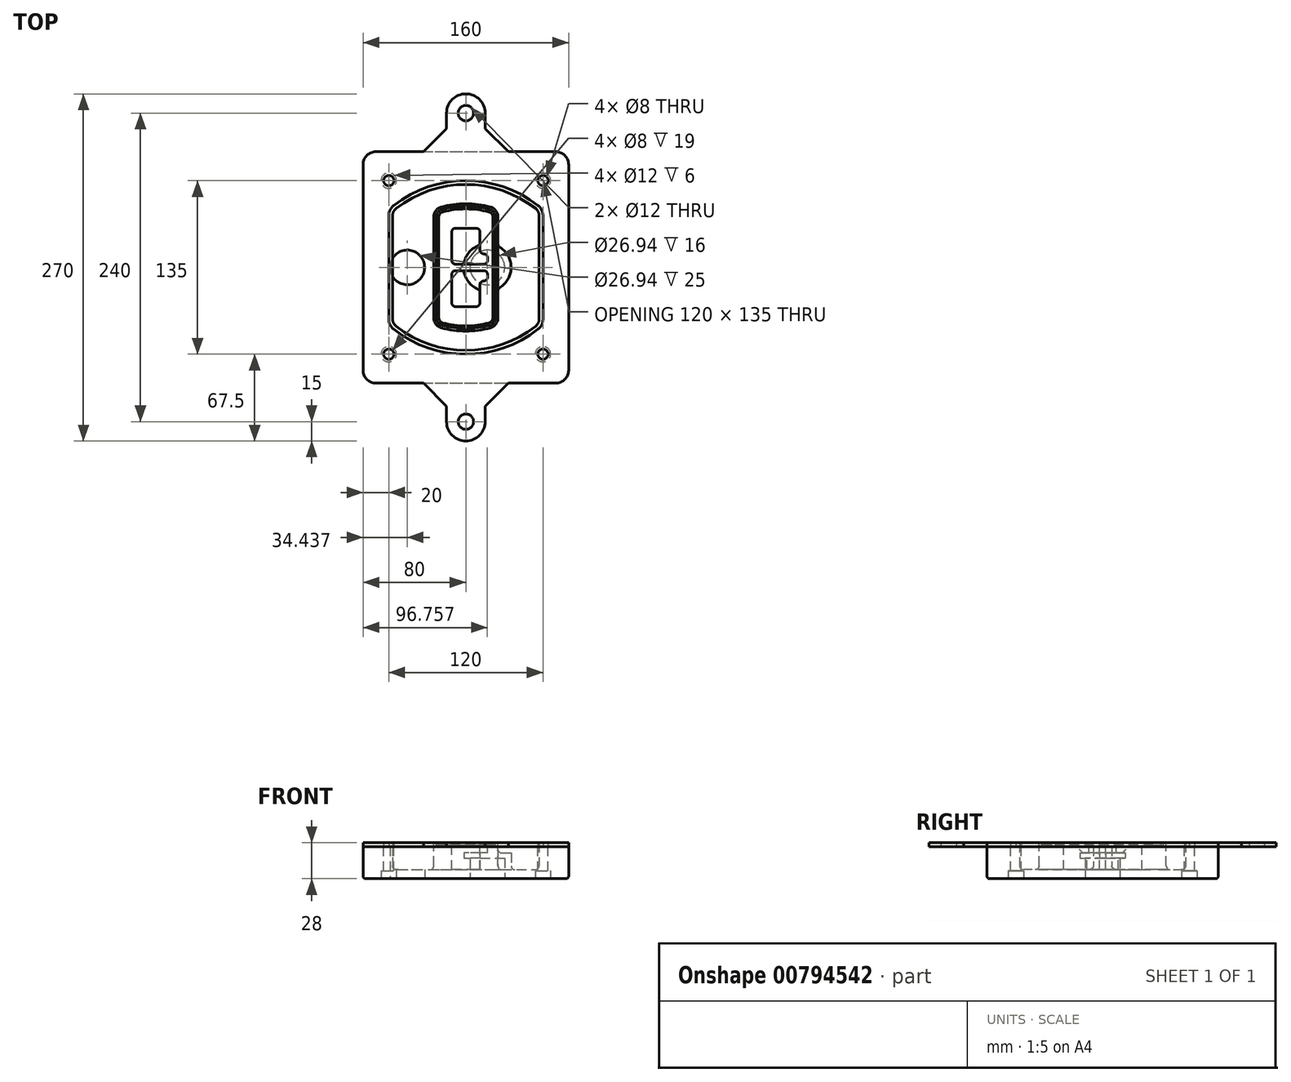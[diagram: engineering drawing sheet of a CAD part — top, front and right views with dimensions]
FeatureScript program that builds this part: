
annotation { "Feature Type Name" : "Feature", "Feature Type Description" : "" }
export const myFeature = defineFeature(function(context is Context, id is Id, definition is map)
    precondition{}
    {
        {
            var Q0;
            Q0=qCreatedBy(makeId("Top.planeOp"),FACE);
            var sketch = newSketch(context, id + "F0", { "sketchPlane" : qUnion([Q0])});
            skPoint(sketch, "E0.rect.middle", {"position": v(0, 0) * mm});
            skLineSegment(sketch, "E1.bottom", {"start": v(-70, -90) * mm, "end": v(70, -90) * mm});
            skLineSegment(sketch, "E1.top", {"start": v(-70, 90) * mm, "end": v(70, 90) * mm});
            skLineSegment(sketch, "E1.left", {"start": v(-80, -80) * mm, "end": v(-80, 80) * mm});
            skLineSegment(sketch, "E1.right", {"start": v(80, -80) * mm, "end": v(80, 80) * mm});
            skLineSegment(sketch, "E2", {"start": v(-80, 90) * mm, "end": v(80, -90) * mm, "construction": true});
            skLineSegment(sketch, "E3", {"start": v(80, 90) * mm, "end": v(-80, -90) * mm, "construction": true});
            skCircle(sketch, "E4", {"center": v(-60, 67.5) * mm, "radius": 4 * mm});
            skCircle(sketch, "E5", {"center": v(60, 67.5) * mm, "radius": 4 * mm});
            skCircle(sketch, "E6", {"center": v(60, -67.5) * mm, "radius": 4 * mm});
            skCircle(sketch, "E7", {"center": v(-60, -67.5) * mm, "radius": 4 * mm});
            skLineSegment(sketch, "E8", {"start": v(-60, 67.5) * mm, "end": v(60, 67.5) * mm, "construction": true});
            skLineSegment(sketch, "E9", {"start": v(60, 67.5) * mm, "end": v(60, -67.5) * mm, "construction": true});
            skLineSegment(sketch, "E10", {"start": v(60, -67.5) * mm, "end": v(-60, -67.5) * mm, "construction": true});
            skLineSegment(sketch, "E11", {"start": v(-60, -67.5) * mm, "end": v(-60, 67.5) * mm, "construction": true});
            skLineSegment(sketch, "E12", {"start": v(-60, 40.3) * mm, "end": v(-60, -40.3) * mm});
            skLineSegment(sketch, "E13", {"start": v(60, 40.3) * mm, "end": v(60, -40.3) * mm});
            skArc(sketch, "E14", {"start": v(56.15, 48.18) * mm, "mid": v(0, 67.5) * mm, "end": v(-56.15, 48.18) * mm});
            skArc(sketch, "E15", {"start": v(-56.15, -48.18) * mm, "mid": v(0, -67.5) * mm, "end": v(56.15, -48.18) * mm});
            skLineSegment(sketch, "E16", {"start": v(-60, 0) * mm, "end": v(60, 0) * mm, "construction": true});
            skPoint(sketch, "E17.visualSharp", {"position": v(-60, -45) * mm});
            skArc(sketch, "E17.filletArc", {"start": v(-60, -40.3) * mm, "mid": v(-58.99, -44.68) * mm, "end": v(-56.15, -48.18) * mm});
            skPoint(sketch, "E18.visualSharp", {"position": v(-60, 45) * mm});
            skArc(sketch, "E18.filletArc", {"start": v(-56.15, 48.18) * mm, "mid": v(-58.99, 44.68) * mm, "end": v(-60, 40.3) * mm});
            skPoint(sketch, "E19.visualSharp", {"position": v(60, 45) * mm});
            skArc(sketch, "E19.filletArc", {"start": v(60, 40.3) * mm, "mid": v(58.99, 44.68) * mm, "end": v(56.15, 48.18) * mm});
            skPoint(sketch, "E20.visualSharp", {"position": v(60, -45) * mm});
            skArc(sketch, "E20.filletArc", {"start": v(56.15, -48.18) * mm, "mid": v(58.99, -44.68) * mm, "end": v(60, -40.3) * mm});
            skPoint(sketch, "E21.visualSharp", {"position": v(-80, 90) * mm});
            skArc(sketch, "E21.filletArc", {"start": v(-70, 90) * mm, "mid": v(-77.07, 87.07) * mm, "end": v(-80, 80) * mm});
            skPoint(sketch, "E22.visualSharp", {"position": v(80, 90) * mm});
            skArc(sketch, "E22.filletArc", {"start": v(80, 80) * mm, "mid": v(77.07, 87.07) * mm, "end": v(70, 90) * mm});
            skPoint(sketch, "E23.visualSharp", {"position": v(80, -90) * mm});
            skArc(sketch, "E23.filletArc", {"start": v(70, -90) * mm, "mid": v(77.07, -87.07) * mm, "end": v(80, -80) * mm});
            skPoint(sketch, "E24.visualSharp", {"position": v(-80, -90) * mm});
            skArc(sketch, "E24.filletArc", {"start": v(-80, -80) * mm, "mid": v(-77.07, -87.07) * mm, "end": v(-70, -90) * mm});
            skArc(sketch, "E25.0", {"start": v(57, 40.3) * mm, "mid": v(56.3, 43.36) * mm, "end": v(54.3, 45.81) * mm});
            skLineSegment(sketch, "E25.1", {"start": v(57, 40.3) * mm, "end": v(57, -40.3) * mm});
            skArc(sketch, "E25.2", {"start": v(54.3, -45.81) * mm, "mid": v(56.3, -43.36) * mm, "end": v(57, -40.3) * mm});
            skArc(sketch, "E25.3", {"start": v(-54.3, -45.81) * mm, "mid": v(0, -64.5) * mm, "end": v(54.3, -45.81) * mm});
            skArc(sketch, "E25.4", {"start": v(-57, -40.3) * mm, "mid": v(-56.3, -43.36) * mm, "end": v(-54.3, -45.81) * mm});
            skArc(sketch, "E25.5", {"start": v(54.3, 45.81) * mm, "mid": v(0, 64.5) * mm, "end": v(-54.3, 45.81) * mm});
            skLineSegment(sketch, "E25.6", {"start": v(-57, 40.3) * mm, "end": v(-57, -40.3) * mm});
            skArc(sketch, "E25.7", {"start": v(-54.3, 45.81) * mm, "mid": v(-56.3, 43.36) * mm, "end": v(-57, 40.3) * mm});
            skArc(sketch, "E26.0", {"start": v(-58.62, 51.33) * mm, "mid": v(-62.58, 46.43) * mm, "end": v(-64, 40.3) * mm});
            skArc(sketch, "E26.1", {"start": v(58.62, 51.33) * mm, "mid": v(0, 71.5) * mm, "end": v(-58.62, 51.33) * mm});
            skArc(sketch, "E26.2", {"start": v(64, 40.3) * mm, "mid": v(62.58, 46.43) * mm, "end": v(58.62, 51.33) * mm});
            skLineSegment(sketch, "E26.3", {"start": v(64, 40.3) * mm, "end": v(64, -40.3) * mm});
            skArc(sketch, "E26.4", {"start": v(58.62, -51.33) * mm, "mid": v(62.58, -46.43) * mm, "end": v(64, -40.3) * mm});
            skLineSegment(sketch, "E26.5", {"start": v(-64, 40.3) * mm, "end": v(-64, -40.3) * mm});
            skArc(sketch, "E26.6", {"start": v(-58.62, -51.33) * mm, "mid": v(0, -71.5) * mm, "end": v(58.62, -51.33) * mm});
            skArc(sketch, "E26.7", {"start": v(-64, -40.3) * mm, "mid": v(-62.58, -46.43) * mm, "end": v(-58.62, -51.33) * mm});
            skSolve(sketch);
        }
        {
            var Q0;
            Q0=makeQuery(id+"F0.imprint","IMPRINT",FACE,{"disambiguationData":[TD([[makeQuery(id+"F0.imprint","IMPRINT",EDGE,{"derivedFrom":sQuery(id+"F0.wireOp",EDGE,"E1.bottom")}),1.0]])]});
            var Q1;
            Q1=makeQuery(id+"F0.imprint","IMPRINT",FACE,{"disambiguationData":[TD([[makeQuery(id+"F0.imprint","IMPRINT",EDGE,{"derivedFrom":sQuery(id+"F0.wireOp",EDGE,"E12")}),1.0]])]});
            var Q2;
            Q2=makeQuery(id+"F0.imprint","IMPRINT",FACE,{"disambiguationData":[TD([[makeQuery(id+"F0.imprint","IMPRINT",EDGE,{"derivedFrom":sQuery(id+"F0.wireOp",EDGE,"E25.0")}),1.0]])]});
            var Q3;
            Q3=makeQuery(id+"F0.imprint","IMPRINT",FACE,{"disambiguationData":[TD([[makeQuery(id+"F0.imprint","IMPRINT",EDGE,{"derivedFrom":sQuery(id+"F0.wireOp",EDGE,"E12")}),-1.0]])]});
            extrude(context, id + "F1", {"entities" : qUnion([Q0, Q1, Q2, Q3]), "oppositeDirection" : true, "depth" : 25 * mm});
        }
        {
            var Q0;
            Q0=makeQuery(id+"F0.imprint","IMPRINT",FACE,{"disambiguationData":[TD([[makeQuery(id+"F0.imprint","IMPRINT",EDGE,{"derivedFrom":sQuery(id+"F0.wireOp",EDGE,"E12")}),1.0]])]});
            extrude(context, id + "F2", {"entities" : qUnion([Q0]), "operationType" : NewBodyOperationType.ADD, "depth" : 3 * mm});
        }
        {
            var Q0;
            Q0=makeQuery(id+"F0.imprint","IMPRINT",FACE,{"disambiguationData":[TD([[makeQuery(id+"F0.imprint","IMPRINT",EDGE,{"derivedFrom":sQuery(id+"F0.wireOp",EDGE,"E25.0")}),1.0]])]});
            extrude(context, id + "F3", {"entities" : qUnion([Q0]), "operationType" : NewBodyOperationType.REMOVE, "oppositeDirection" : true, "depth" : 18 * mm});
        }
        {
            var Q0;
            Q0=makeQuery(id+"F2.opExtrude","CAP_FACE",FACE,{"disambiguationData":[OSD([sQuery(id+"F0.wireOp",EDGE,"E12"),sQuery(id+"F0.wireOp",EDGE,"E13"),sQuery(id+"F0.wireOp",EDGE,"E14"),sQuery(id+"F0.wireOp",EDGE,"E15"),sQuery(id+"F0.wireOp",EDGE,"E17.filletArc"),sQuery(id+"F0.wireOp",EDGE,"E18.filletArc"),sQuery(id+"F0.wireOp",EDGE,"E19.filletArc"),sQuery(id+"F0.wireOp",EDGE,"E20.filletArc"),sQuery(id+"F0.wireOp",EDGE,"E25.0"),sQuery(id+"F0.wireOp",EDGE,"E25.1"),sQuery(id+"F0.wireOp",EDGE,"E25.2"),sQuery(id+"F0.wireOp",EDGE,"E25.3"),sQuery(id+"F0.wireOp",EDGE,"E25.4"),sQuery(id+"F0.wireOp",EDGE,"E25.5"),sQuery(id+"F0.wireOp",EDGE,"E25.6"),sQuery(id+"F0.wireOp",EDGE,"E25.7")])],"isStart":false});
            var sketch = newSketch(context, id + "F4", { "sketchPlane" : qUnion([Q0])});
            skArc(sketch, "E27.0", {"start": v(-19.08, -46.97) * mm, "mid": v(0, -49.5) * mm, "end": v(19.08, -46.97) * mm});
            skArc(sketch, "E28.0", {"start": v(19.08, 46.97) * mm, "mid": v(0, 49.5) * mm, "end": v(-19.08, 46.97) * mm});
            skLineSegment(sketch, "E29", {"start": v(-25, 39.25) * mm, "end": v(-25, -39.25) * mm});
            skLineSegment(sketch, "E30", {"start": v(25, 39.25) * mm, "end": v(25, -39.25) * mm});
            skLineSegment(sketch, "E31", {"start": v(-25, 45.1) * mm, "end": v(25, 45.1) * mm, "construction": true});
            skLineSegment(sketch, "E32", {"start": v(-25, -45.1) * mm, "end": v(25, -45.1) * mm, "construction": true});
            skPoint(sketch, "E33.visualSharp", {"position": v(-25, 45.1) * mm});
            skArc(sketch, "E33.filletArc", {"start": v(-19.08, 46.97) * mm, "mid": v(-23.35, 44.11) * mm, "end": v(-25, 39.25) * mm});
            skPoint(sketch, "E34.visualSharp", {"position": v(25, 45.1) * mm});
            skArc(sketch, "E34.filletArc", {"start": v(25, 39.25) * mm, "mid": v(23.35, 44.11) * mm, "end": v(19.08, 46.97) * mm});
            skPoint(sketch, "E35.visualSharp", {"position": v(25, -45.1) * mm});
            skArc(sketch, "E35.filletArc", {"start": v(19.08, -46.97) * mm, "mid": v(23.35, -44.11) * mm, "end": v(25, -39.25) * mm});
            skPoint(sketch, "E36.visualSharp", {"position": v(-25, -45.1) * mm});
            skArc(sketch, "E36.filletArc", {"start": v(-25, -39.25) * mm, "mid": v(-23.35, -44.11) * mm, "end": v(-19.08, -46.97) * mm});
            skArc(sketch, "E37.0", {"start": v(54.3, 45.81) * mm, "mid": v(0, 64.5) * mm, "end": v(-54.3, 45.81) * mm});
            skArc(sketch, "E37.1", {"start": v(-54.3, 45.81) * mm, "mid": v(-56.3, 43.36) * mm, "end": v(-57, 40.3) * mm});
            skLineSegment(sketch, "E37.2", {"start": v(-57, 40.3) * mm, "end": v(-57, -40.3) * mm});
            skArc(sketch, "E37.3", {"start": v(-57, -40.3) * mm, "mid": v(-56.3, -43.36) * mm, "end": v(-54.3, -45.81) * mm});
            skArc(sketch, "E37.4", {"start": v(-54.3, -45.81) * mm, "mid": v(0, -64.5) * mm, "end": v(54.3, -45.81) * mm});
            skArc(sketch, "E37.5", {"start": v(54.3, -45.81) * mm, "mid": v(56.3, -43.36) * mm, "end": v(57, -40.3) * mm});
            skLineSegment(sketch, "E37.6", {"start": v(57, 40.3) * mm, "end": v(57, -40.3) * mm});
            skArc(sketch, "E37.7", {"start": v(57, 40.3) * mm, "mid": v(56.3, 43.36) * mm, "end": v(54.3, 45.81) * mm});
            skLineSegment(sketch, "E38.0", {"start": v(23, 39.25) * mm, "end": v(23, -39.25) * mm});
            skArc(sketch, "E38.1", {"start": v(18.56, -45.04) * mm, "mid": v(21.76, -42.9) * mm, "end": v(23, -39.25) * mm});
            skArc(sketch, "E38.2", {"start": v(-18.56, -45.04) * mm, "mid": v(0, -47.5) * mm, "end": v(18.56, -45.04) * mm});
            skArc(sketch, "E38.3", {"start": v(-23, -39.25) * mm, "mid": v(-21.76, -42.9) * mm, "end": v(-18.56, -45.04) * mm});
            skLineSegment(sketch, "E38.4", {"start": v(-23, 39.25) * mm, "end": v(-23, -39.25) * mm});
            skArc(sketch, "E38.5", {"start": v(23, 39.25) * mm, "mid": v(21.76, 42.9) * mm, "end": v(18.56, 45.04) * mm});
            skArc(sketch, "E38.6", {"start": v(-18.56, 45.04) * mm, "mid": v(-21.76, 42.9) * mm, "end": v(-23, 39.25) * mm});
            skArc(sketch, "E38.7", {"start": v(18.56, 45.04) * mm, "mid": v(0, 47.5) * mm, "end": v(-18.56, 45.04) * mm});
            skArc(sketch, "E39.0", {"start": v(21, 39.25) * mm, "mid": v(20.18, 41.68) * mm, "end": v(18.04, 43.1) * mm});
            skLineSegment(sketch, "E39.1", {"start": v(21, 39.25) * mm, "end": v(21, -39.25) * mm});
            skArc(sketch, "E39.2", {"start": v(18.04, -43.1) * mm, "mid": v(20.18, -41.68) * mm, "end": v(21, -39.25) * mm});
            skArc(sketch, "E39.3", {"start": v(-18.04, -43.1) * mm, "mid": v(0, -45.5) * mm, "end": v(18.04, -43.1) * mm});
            skArc(sketch, "E39.4", {"start": v(-21, -39.25) * mm, "mid": v(-20.18, -41.68) * mm, "end": v(-18.04, -43.1) * mm});
            skArc(sketch, "E39.5", {"start": v(18.04, 43.1) * mm, "mid": v(0, 45.5) * mm, "end": v(-18.04, 43.1) * mm});
            skLineSegment(sketch, "E39.6", {"start": v(-21, 39.25) * mm, "end": v(-21, -39.25) * mm});
            skArc(sketch, "E39.7", {"start": v(-18.04, 43.1) * mm, "mid": v(-20.18, 41.68) * mm, "end": v(-21, 39.25) * mm});
            skLineSegment(sketch, "E40", {"start": v(-25, 0) * mm, "end": v(25, 0) * mm, "construction": true});
            skLineSegment(sketch, "E41", {"start": v(-11, 5.5) * mm, "end": v(-11, 27.5) * mm});
            skLineSegment(sketch, "E42", {"start": v(-8, 30.5) * mm, "end": v(8, 30.5) * mm});
            skLineSegment(sketch, "E43", {"start": v(11, 27.5) * mm, "end": v(11, 13.5) * mm});
            skLineSegment(sketch, "E44", {"start": v(14, 10.5) * mm, "end": v(14, 10.5) * mm});
            skLineSegment(sketch, "E45", {"start": v(17, 7.5) * mm, "end": v(17, 5.5) * mm});
            skLineSegment(sketch, "E46", {"start": v(14, 2.5) * mm, "end": v(-8, 2.5) * mm});
            skPoint(sketch, "E47.visualSharp", {"position": v(-11, 30.5) * mm});
            skArc(sketch, "E47.filletArc", {"start": v(-8, 30.5) * mm, "mid": v(-10.12, 29.62) * mm, "end": v(-11, 27.5) * mm});
            skPoint(sketch, "E48.visualSharp", {"position": v(11, 30.5) * mm});
            skArc(sketch, "E48.filletArc", {"start": v(11, 27.5) * mm, "mid": v(10.12, 29.62) * mm, "end": v(8, 30.5) * mm});
            skPoint(sketch, "E49.visualSharp", {"position": v(11, 10.5) * mm});
            skArc(sketch, "E49.filletArc", {"start": v(11, 13.5) * mm, "mid": v(11.88, 11.38) * mm, "end": v(14, 10.5) * mm});
            skPoint(sketch, "E50.visualSharp", {"position": v(17, 10.5) * mm});
            skArc(sketch, "E50.filletArc", {"start": v(17, 7.5) * mm, "mid": v(16.12, 9.62) * mm, "end": v(14, 10.5) * mm});
            skPoint(sketch, "E51.visualSharp", {"position": v(17, 2.5) * mm});
            skArc(sketch, "E51.filletArc", {"start": v(14, 2.5) * mm, "mid": v(16.12, 3.38) * mm, "end": v(17, 5.5) * mm});
            skPoint(sketch, "E52.visualSharp", {"position": v(-11, 2.5) * mm});
            skArc(sketch, "E52.filletArc", {"start": v(-11, 5.5) * mm, "mid": v(-10.12, 3.38) * mm, "end": v(-8, 2.5) * mm});
            skLineSegment(sketch, "E53.0.MirrorCS", {"start": v(14, -2.5) * mm, "end": v(-8, -2.5) * mm});
            skArc(sketch, "E54.0.MirrorCS", {"start": v(-11, -5.5) * mm, "mid": v(-10.12, -3.38) * mm, "end": v(-8, -2.5) * mm});
            skLineSegment(sketch, "E55.0.MirrorCS", {"start": v(-11, -5.5) * mm, "end": v(-11, -27.5) * mm});
            skArc(sketch, "E56.0.MirrorCS", {"start": v(-8, -30.5) * mm, "mid": v(-10.12, -29.62) * mm, "end": v(-11, -27.5) * mm});
            skLineSegment(sketch, "E57.0.MirrorCS", {"start": v(-8, -30.5) * mm, "end": v(8, -30.5) * mm});
            skArc(sketch, "E58.0.MirrorCS", {"start": v(11, -27.5) * mm, "mid": v(10.12, -29.62) * mm, "end": v(8, -30.5) * mm});
            skLineSegment(sketch, "E59.0.MirrorCS", {"start": v(11, -27.5) * mm, "end": v(11, -13.5) * mm});
            skArc(sketch, "E60.0.MirrorCS", {"start": v(11, -13.5) * mm, "mid": v(11.88, -11.38) * mm, "end": v(14, -10.5) * mm});
            skArc(sketch, "E61.0.MirrorCS", {"start": v(17, -7.5) * mm, "mid": v(16.12, -9.62) * mm, "end": v(14, -10.5) * mm});
            skLineSegment(sketch, "E62.0.MirrorCS", {"start": v(17, -7.5) * mm, "end": v(17, -5.5) * mm});
            skArc(sketch, "E63.0.MirrorCS", {"start": v(14, -2.5) * mm, "mid": v(16.12, -3.38) * mm, "end": v(17, -5.5) * mm});
            skSolve(sketch);
        }
        {
            var Q0;
            Q0=makeQuery(id+"F4.imprint","IMPRINT",FACE,{"disambiguationData":[TD([[makeQuery(id+"F4.imprint","IMPRINT",EDGE,{"derivedFrom":sQuery(id+"F4.wireOp",EDGE,"E27.0")}),1.0]])]});
            var Q1;
            Q1=makeQuery(id+"F4.imprint","IMPRINT",FACE,{"disambiguationData":[TD([[makeQuery(id+"F4.imprint","IMPRINT",EDGE,{"derivedFrom":sQuery(id+"F4.wireOp",EDGE,"E38.0")}),-1.0]])]});
            var Q2;
            Q2=makeQuery(id+"F4.imprint","IMPRINT",FACE,{"disambiguationData":[TD([[makeQuery(id+"F4.imprint","IMPRINT",EDGE,{"derivedFrom":sQuery(id+"F4.wireOp",EDGE,"E39.0")}),1.0]])]});
            extrude(context, id + "F5", {"entities" : qUnion([Q0, Q1, Q2]), "operationType" : NewBodyOperationType.ADD, "endBound" : BoundingType.UP_TO_NEXT, "oppositeDirection" : true, "depth" : 25 * mm});
        }
        {
            var Q0;
            Q0=makeQuery(id+"F4.imprint","IMPRINT",FACE,{"disambiguationData":[TD([[makeQuery(id+"F4.imprint","IMPRINT",EDGE,{"derivedFrom":sQuery(id+"F4.wireOp",EDGE,"E38.0")}),-1.0]])]});
            extrude(context, id + "F6", {"entities" : qUnion([Q0]), "operationType" : NewBodyOperationType.REMOVE, "oppositeDirection" : true, "depth" : 2 * mm});
        }
        {
            var Q0;
            Q0=makeQuery(id+"F1.opExtrude","CAP_FACE",FACE,{"disambiguationData":[OSD([sQuery(id+"F0.wireOp",EDGE,"E1.bottom"),sQuery(id+"F0.wireOp",EDGE,"E1.top"),sQuery(id+"F0.wireOp",EDGE,"E1.left"),sQuery(id+"F0.wireOp",EDGE,"E1.right"),sQuery(id+"F0.wireOp",EDGE,"E4"),sQuery(id+"F0.wireOp",EDGE,"E5"),sQuery(id+"F0.wireOp",EDGE,"E6"),sQuery(id+"F0.wireOp",EDGE,"E7"),sQuery(id+"F0.wireOp",EDGE,"E21.filletArc"),sQuery(id+"F0.wireOp",EDGE,"E22.filletArc"),sQuery(id+"F0.wireOp",EDGE,"E23.filletArc"),sQuery(id+"F0.wireOp",EDGE,"E24.filletArc")])],"isStart":false});
            var sketch = newSketch(context, id + "F7", { "sketchPlane" : qUnion([Q0])});
            skCircle(sketch, "E64", {"center": v(16.76, 0) * mm, "radius": 13.47 * mm});
            skCircle(sketch, "E65", {"center": v(-45.56, 0) * mm, "radius": 13.47 * mm});
            skLineSegment(sketch, "E66", {"start": v(80, 0) * mm, "end": v(-80, 0) * mm});
            skCircle(sketch, "E67", {"center": v(16.76, 0) * mm, "radius": 18.47 * mm});
            skCircle(sketch, "E68", {"center": v(60, -67.5) * mm, "radius": 6 * mm});
            skCircle(sketch, "E69", {"center": v(-60, -67.5) * mm, "radius": 6 * mm});
            skCircle(sketch, "E70", {"center": v(-60, 67.5) * mm, "radius": 6 * mm});
            skCircle(sketch, "E71", {"center": v(60, 67.5) * mm, "radius": 6 * mm});
            skSolve(sketch);
        }
        {
            var Q0;
            {var subQ1=sQuery(id+"F7.wireOp",EDGE,"E66");var subQ4=sQuery(id+"F7.wireOp",EDGE,"E64");var subQ6=makeQuery(id+"F7.imprint","INTERSECT",VERTEX,{"disambiguationData":[OD(0.0)],"derivedFrom":[subQ4,subQ1]});Q0=makeQuery(id+"F7.imprint","IMPRINT",FACE,{"disambiguationData":[TD([[makeQuery(id+"F7.imprint","IMPRINT",EDGE,{"disambiguationData":[TD([[subQ6,-1.0]])],"derivedFrom":subQ4}),-1.0]])]});}
            var Q1;
            {var subQ0=sQuery(id+"F7.wireOp",EDGE,"E66");var subQ1=sQuery(id+"F7.wireOp",EDGE,"E64");var subQ3=makeQuery(id+"F7.imprint","INTERSECT",VERTEX,{"disambiguationData":[OD(0.0)],"derivedFrom":[subQ1,subQ0]});Q1=makeQuery(id+"F7.imprint","IMPRINT",FACE,{"disambiguationData":[TD([[makeQuery(id+"F7.imprint","IMPRINT",EDGE,{"disambiguationData":[TD([[subQ3,-1.0]])],"derivedFrom":subQ1}),1.0]])]});}
            var Q2;
            {var subQ0=sQuery(id+"F7.wireOp",EDGE,"E66");var subQ1=sQuery(id+"F7.wireOp",EDGE,"E64");var subQ3=makeQuery(id+"F7.imprint","INTERSECT",VERTEX,{"disambiguationData":[OD(0.0)],"derivedFrom":[subQ1,subQ0]});Q2=makeQuery(id+"F7.imprint","IMPRINT",FACE,{"disambiguationData":[TD([[makeQuery(id+"F7.imprint","IMPRINT",EDGE,{"disambiguationData":[TD([[subQ3,1.0]])],"derivedFrom":subQ1}),1.0]])]});}
            var Q3;
            {var subQ1=sQuery(id+"F7.wireOp",EDGE,"E66");var subQ4=sQuery(id+"F7.wireOp",EDGE,"E64");var subQ6=makeQuery(id+"F7.imprint","INTERSECT",VERTEX,{"disambiguationData":[OD(0.0)],"derivedFrom":[subQ4,subQ1]});Q3=makeQuery(id+"F7.imprint","IMPRINT",FACE,{"disambiguationData":[TD([[makeQuery(id+"F7.imprint","IMPRINT",EDGE,{"disambiguationData":[TD([[subQ6,1.0]])],"derivedFrom":subQ4}),-1.0]])]});}
            extrude(context, id + "F8", {"entities" : qUnion([Q0, Q1, Q2, Q3]), "operationType" : NewBodyOperationType.ADD, "oppositeDirection" : true, "depth" : 20 * mm});
        }
        {
            var Q0;
            {var subQ0=sQuery(id+"F7.wireOp",EDGE,"E66");var subQ1=sQuery(id+"F7.wireOp",EDGE,"E64");var subQ3=makeQuery(id+"F7.imprint","INTERSECT",VERTEX,{"disambiguationData":[OD(0.0)],"derivedFrom":[subQ1,subQ0]});Q0=makeQuery(id+"F7.imprint","IMPRINT",FACE,{"disambiguationData":[TD([[makeQuery(id+"F7.imprint","IMPRINT",EDGE,{"disambiguationData":[TD([[subQ3,-1.0]])],"derivedFrom":subQ1}),1.0]])]});}
            var Q1;
            {var subQ0=sQuery(id+"F7.wireOp",EDGE,"E66");var subQ1=sQuery(id+"F7.wireOp",EDGE,"E64");var subQ3=makeQuery(id+"F7.imprint","INTERSECT",VERTEX,{"disambiguationData":[OD(0.0)],"derivedFrom":[subQ1,subQ0]});Q1=makeQuery(id+"F7.imprint","IMPRINT",FACE,{"disambiguationData":[TD([[makeQuery(id+"F7.imprint","IMPRINT",EDGE,{"disambiguationData":[TD([[subQ3,1.0]])],"derivedFrom":subQ1}),1.0]])]});}
            extrude(context, id + "F9", {"entities" : qUnion([Q0, Q1]), "operationType" : NewBodyOperationType.REMOVE, "oppositeDirection" : true, "depth" : 16 * mm});
        }
        {
            var Q0;
            {var subQ0=sQuery(id+"F7.wireOp",EDGE,"E66");var subQ1=sQuery(id+"F7.wireOp",EDGE,"E65");var subQ3=makeQuery(id+"F7.imprint","INTERSECT",VERTEX,{"disambiguationData":[OD(0.0)],"derivedFrom":[subQ1,subQ0]});Q0=makeQuery(id+"F7.imprint","IMPRINT",FACE,{"disambiguationData":[TD([[makeQuery(id+"F7.imprint","IMPRINT",EDGE,{"disambiguationData":[TD([[subQ3,-1.0]])],"derivedFrom":subQ1}),1.0]])]});}
            var Q1;
            {var subQ0=sQuery(id+"F7.wireOp",EDGE,"E66");var subQ1=sQuery(id+"F7.wireOp",EDGE,"E65");var subQ3=makeQuery(id+"F7.imprint","INTERSECT",VERTEX,{"disambiguationData":[OD(0.0)],"derivedFrom":[subQ1,subQ0]});Q1=makeQuery(id+"F7.imprint","IMPRINT",FACE,{"disambiguationData":[TD([[makeQuery(id+"F7.imprint","IMPRINT",EDGE,{"disambiguationData":[TD([[subQ3,1.0]])],"derivedFrom":subQ1}),1.0]])]});}
            extrude(context, id + "F10", {"entities" : qUnion([Q0, Q1]), "operationType" : NewBodyOperationType.REMOVE, "oppositeDirection" : true, "depth" : 25 * mm});
        }
        {
            var Q0;
            Q0=makeQuery(id+"F7.imprint","IMPRINT",FACE,{"disambiguationData":[TD([[makeQuery(id+"F7.imprint","IMPRINT",EDGE,{"derivedFrom":sQuery(id+"F7.wireOp",EDGE,"E68")}),1.0]])]});
            var Q1;
            Q1=makeQuery(id+"F7.imprint","IMPRINT",FACE,{"disambiguationData":[TD([[makeQuery(id+"F7.imprint","IMPRINT",EDGE,{"derivedFrom":makeQuery(id+"F1.opExtrude","CAP_EDGE",EDGE,{"disambiguationData":[OSD([sQuery(id+"F0.wireOp",EDGE,"E5")])],"isStart":false})}),-1.0]])]});
            var Q2;
            Q2=makeQuery(id+"F7.imprint","IMPRINT",FACE,{"disambiguationData":[TD([[makeQuery(id+"F7.imprint","IMPRINT",EDGE,{"derivedFrom":sQuery(id+"F7.wireOp",EDGE,"E69")}),1.0]])]});
            var Q3;
            Q3=makeQuery(id+"F7.imprint","IMPRINT",FACE,{"disambiguationData":[TD([[makeQuery(id+"F7.imprint","IMPRINT",EDGE,{"derivedFrom":makeQuery(id+"F1.opExtrude","CAP_EDGE",EDGE,{"disambiguationData":[OSD([sQuery(id+"F0.wireOp",EDGE,"E4")])],"isStart":false})}),-1.0]])]});
            var Q4;
            Q4=makeQuery(id+"F7.imprint","IMPRINT",FACE,{"disambiguationData":[TD([[makeQuery(id+"F7.imprint","IMPRINT",EDGE,{"derivedFrom":sQuery(id+"F7.wireOp",EDGE,"E70")}),1.0]])]});
            var Q5;
            Q5=makeQuery(id+"F7.imprint","IMPRINT",FACE,{"disambiguationData":[TD([[makeQuery(id+"F7.imprint","IMPRINT",EDGE,{"derivedFrom":makeQuery(id+"F1.opExtrude","CAP_EDGE",EDGE,{"disambiguationData":[OSD([sQuery(id+"F0.wireOp",EDGE,"E7")])],"isStart":false})}),-1.0]])]});
            var Q6;
            Q6=makeQuery(id+"F7.imprint","IMPRINT",FACE,{"disambiguationData":[TD([[makeQuery(id+"F7.imprint","IMPRINT",EDGE,{"derivedFrom":sQuery(id+"F7.wireOp",EDGE,"E71")}),1.0]])]});
            var Q7;
            Q7=makeQuery(id+"F7.imprint","IMPRINT",FACE,{"disambiguationData":[TD([[makeQuery(id+"F7.imprint","IMPRINT",EDGE,{"derivedFrom":makeQuery(id+"F1.opExtrude","CAP_EDGE",EDGE,{"disambiguationData":[OSD([sQuery(id+"F0.wireOp",EDGE,"E6")])],"isStart":false})}),-1.0]])]});
            extrude(context, id + "F11", {"entities" : qUnion([Q0, Q1, Q2, Q3, Q4, Q5, Q6, Q7]), "operationType" : NewBodyOperationType.REMOVE, "oppositeDirection" : true, "depth" : 6 * mm});
        }
        {
            var Q0;
            Q0=makeQuery(id+"F9.boolean.opBoolean","COPY",FACE,{"derivedFrom":makeQuery(id+"F9.opExtrude","CAP_FACE",FACE,{"disambiguationData":[OSD([sQuery(id+"F7.wireOp",EDGE,"E64")])],"isStart":false})});
            var sketch = newSketch(context, id + "F12", { "sketchPlane" : qUnion([Q0])});
            skArc(sketch, "E72.0", {"start": v(11, 17.55) * mm, "mid": v(2.57, 11.82) * mm, "end": v(-1.54, 2.5) * mm});
            skArc(sketch, "E72.1", {"start": v(-1.54, -2.5) * mm, "mid": v(2.57, -11.82) * mm, "end": v(11, -17.55) * mm});
            skLineSegment(sketch, "E73", {"start": v(-1.54, -2.5) * mm, "end": v(14, -2.5) * mm});
            skLineSegment(sketch, "E74.0", {"start": v(14, 2.5) * mm, "end": v(-1.54, 2.5) * mm});
            skArc(sketch, "E74.1", {"start": v(14, 2.5) * mm, "mid": v(16.12, 3.38) * mm, "end": v(17, 5.5) * mm});
            skLineSegment(sketch, "E74.2", {"start": v(17, 7.5) * mm, "end": v(17, 5.5) * mm});
            skArc(sketch, "E74.3", {"start": v(17, 7.5) * mm, "mid": v(16.12, 9.62) * mm, "end": v(14, 10.5) * mm});
            skArc(sketch, "E74.4", {"start": v(11, 13.5) * mm, "mid": v(11.88, 11.38) * mm, "end": v(14, 10.5) * mm});
            skLineSegment(sketch, "E74.5", {"start": v(11, 17.55) * mm, "end": v(11, 13.5) * mm});
            skLineSegment(sketch, "E74.7", {"start": v(14, -2.5) * mm, "end": v(-1.54, -2.5) * mm});
            skArc(sketch, "E74.8", {"start": v(14, -2.5) * mm, "mid": v(16.12, -3.38) * mm, "end": v(17, -5.5) * mm});
            skLineSegment(sketch, "E74.9", {"start": v(17, -7.5) * mm, "end": v(17, -5.5) * mm});
            skArc(sketch, "E74.10", {"start": v(17, -7.5) * mm, "mid": v(16.12, -9.62) * mm, "end": v(14, -10.5) * mm});
            skArc(sketch, "E74.11", {"start": v(11, -13.5) * mm, "mid": v(11.88, -11.38) * mm, "end": v(14, -10.5) * mm});
            skLineSegment(sketch, "E74.12", {"start": v(11, -17.55) * mm, "end": v(11, -13.5) * mm});
            skPoint(sketch, "E75.orphan", {"position": v(11, -27.5) * mm});
            skPoint(sketch, "E76.orphan", {"position": v(-8, -2.5) * mm});
            skPoint(sketch, "E77.orphan", {"position": v(-8, 2.5) * mm});
            skPoint(sketch, "E78.orphan", {"position": v(11, 27.5) * mm});
            skSolve(sketch);
        }
        {
            var Q0;
            {var subQ7=sQuery(id+"F12.wireOp",EDGE,"E72.0");var subQ14=sQuery(id+"F12.wireOp",EDGE,"E72.1");var subQ16=sQuery(id+"F12.wireOp",EDGE,"E74.1");var subQ18=sQuery(id+"F12.wireOp",EDGE,"E74.8");Q0=qUnion([makeQuery(id+"F12.imprint","IMPRINT",FACE,{"disambiguationData":[TD([[makeQuery(id+"F12.imprint","IMPRINT",EDGE,{"derivedFrom":subQ7}),1.0]])]}),makeQuery(id+"F12.imprint","IMPRINT",FACE,{"disambiguationData":[TD([[makeQuery(id+"F12.imprint","IMPRINT",EDGE,{"derivedFrom":subQ14}),1.0]])]}),makeQuery(id+"F12.imprint","IMPRINT",FACE,{"disambiguationData":[TD([[makeQuery(id+"F12.imprint","IMPRINT",EDGE,{"derivedFrom":subQ16}),1.0]])]}),makeQuery(id+"F12.imprint","IMPRINT",FACE,{"disambiguationData":[TD([[makeQuery(id+"F12.imprint","IMPRINT",EDGE,{"derivedFrom":subQ18}),-1.0]])]})]);}
            var Q1;
            Q1=makeQuery(id+"F5.boolean.opBoolean","SPLIT",FACE,{"disambiguationData":[TD([makeQuery(id+"F5.opExtrude","SWEPT_FACE",FACE,{"disambiguationData":[OSD([sQuery(id+"F4.wireOp",EDGE,"E41")])]})])],"derivedFrom":makeQuery(id+"F3.boolean.opBoolean","COPY",FACE,{"derivedFrom":makeQuery(id+"F3.opExtrude","CAP_FACE",FACE,{"disambiguationData":[OSD([sQuery(id+"F0.wireOp",EDGE,"E25.0"),sQuery(id+"F0.wireOp",EDGE,"E25.1"),sQuery(id+"F0.wireOp",EDGE,"E25.2"),sQuery(id+"F0.wireOp",EDGE,"E25.3"),sQuery(id+"F0.wireOp",EDGE,"E25.4"),sQuery(id+"F0.wireOp",EDGE,"E25.5"),sQuery(id+"F0.wireOp",EDGE,"E25.6"),sQuery(id+"F0.wireOp",EDGE,"E25.7")])],"isStart":false})})});
            extrude(context, id + "F13", {"entities" : qUnion([Q0]), "operationType" : NewBodyOperationType.REMOVE, "endBound" : BoundingType.UP_TO_SURFACE, "endBoundEntityFace" : qUnion([Q1]), "depth" : 25 * mm});
        }
        {
            var Q0;
            Q0=makeQuery(id+"F3.boolean.opBoolean","COPY",EDGE,{"derivedFrom":makeQuery(id+"F3.opExtrude","CAP_EDGE",EDGE,{"disambiguationData":[OSD([sQuery(id+"F0.wireOp",EDGE,"E25.6")])],"isStart":false})});
            var Q1;
            Q1=makeQuery(id+"F8.boolean.opBoolean","INTERSECT",EDGE,{"derivedFrom":[makeQuery(id+"F5.opExtrude","SWEPT_FACE",FACE,{"disambiguationData":[OSD([sQuery(id+"F4.wireOp",EDGE,"E30")])]}),makeQuery(id+"F8.opExtrude","CAP_FACE",FACE,{"disambiguationData":[OSD([sQuery(id+"F7.wireOp",EDGE,"E67")])],"isStart":false})]});
            var Q2;
            Q2=makeQuery(id+"F8.boolean.opBoolean","INTERSECT",EDGE,{"disambiguationData":[OD(1.0)],"derivedFrom":[makeQuery(id+"F5.opExtrude","SWEPT_FACE",FACE,{"disambiguationData":[OSD([sQuery(id+"F4.wireOp",EDGE,"E30")])]}),makeQuery(id+"F8.opExtrude","SWEPT_FACE",FACE,{"disambiguationData":[OSD([sQuery(id+"F7.wireOp",EDGE,"E67")])]})]});
            var Q3;
            {var subQ0=sQuery(id+"F4.wireOp",EDGE,"E30");Q3=makeQuery(id+"F8.boolean.opBoolean","SPLIT",EDGE,{"disambiguationData":[TD([makeQuery(id+"F5.opExtrude","SWEPT_FACE",FACE,{"disambiguationData":[OSD([sQuery(id+"F4.wireOp",EDGE,"E35.filletArc")])]})])],"derivedFrom":makeQuery(id+"F5.opExtrude","CAP_EDGE",EDGE,{"disambiguationData":[OSD([subQ0])],"isStart":false})});}
            var Q4;
            {var subQ0=sQuery(id+"F0.wireOp",EDGE,"E25.7");var subQ1=sQuery(id+"F0.wireOp",EDGE,"E25.1");var subQ2=sQuery(id+"F0.wireOp",EDGE,"E25.6");var subQ3=sQuery(id+"F0.wireOp",EDGE,"E25.5");var subQ4=sQuery(id+"F0.wireOp",EDGE,"E25.4");var subQ5=sQuery(id+"F0.wireOp",EDGE,"E25.0");var subQ6=sQuery(id+"F0.wireOp",EDGE,"E25.2");var subQ7=sQuery(id+"F0.wireOp",EDGE,"E25.3");Q4=makeQuery(id+"F8.boolean.opBoolean","INTERSECT",EDGE,{"derivedFrom":[makeQuery(id+"F5.boolean.opBoolean","SPLIT",FACE,{"disambiguationData":[TD([makeQuery(id+"F2.opExtrude","SWEPT_FACE",FACE,{"disambiguationData":[OSD([subQ5])]})])],"derivedFrom":makeQuery(id+"F3.boolean.opBoolean","COPY",FACE,{"derivedFrom":makeQuery(id+"F3.opExtrude","CAP_FACE",FACE,{"disambiguationData":[OSD([subQ5,subQ1,subQ6,subQ7,subQ4,subQ3,subQ2,subQ0])],"isStart":false})})}),makeQuery(id+"F8.opExtrude","SWEPT_FACE",FACE,{"disambiguationData":[OSD([sQuery(id+"F7.wireOp",EDGE,"E67")])]})]});}
            var Q5;
            Q5=makeQuery(id+"F8.boolean.opBoolean","INTERSECT",EDGE,{"disambiguationData":[OD(0.0)],"derivedFrom":[makeQuery(id+"F5.opExtrude","SWEPT_FACE",FACE,{"disambiguationData":[OSD([sQuery(id+"F4.wireOp",EDGE,"E30")])]}),makeQuery(id+"F8.opExtrude","SWEPT_FACE",FACE,{"disambiguationData":[OSD([sQuery(id+"F7.wireOp",EDGE,"E67")])]})]});
            fillet(context, id + "F14", {"entities" : qUnion([Q0, Q1, Q2, Q3, Q4, Q5]), "radius" : 3 * mm, "tangentPropagation" : true, "allowEdgeOverflow" : false});
        }
        {
            var Q0;
            Q0=makeQuery(id+"F1.opExtrude","CAP_EDGE",EDGE,{"disambiguationData":[OSD([sQuery(id+"F0.wireOp",EDGE,"E1.bottom")])],"isStart":false});
            fillet(context, id + "F15", {"entities" : qUnion([Q0]), "radius" : 2 * mm, "tangentPropagation" : true, "allowEdgeOverflow" : false});
        }
        {
            var Q0;
            {var subQ0=sQuery(id+"F0.wireOp",EDGE,"E21.filletArc");var subQ1=sQuery(id+"F0.wireOp",EDGE,"E7");var subQ2=sQuery(id+"F0.wireOp",EDGE,"E6");var subQ3=sQuery(id+"F0.wireOp",EDGE,"E5");var subQ4=sQuery(id+"F0.wireOp",EDGE,"E4");var subQ5=sQuery(id+"F0.wireOp",EDGE,"E22.filletArc");var subQ6=sQuery(id+"F0.wireOp",EDGE,"E1.bottom");var subQ7=sQuery(id+"F0.wireOp",EDGE,"E1.right");var subQ8=sQuery(id+"F0.wireOp",EDGE,"E1.top");var subQ9=sQuery(id+"F0.wireOp",EDGE,"E1.left");var subQ10=sQuery(id+"F0.wireOp",EDGE,"E23.filletArc");var subQ11=sQuery(id+"F0.wireOp",EDGE,"E24.filletArc");Q0=makeQuery(id+"F2.boolean.opBoolean","SPLIT",FACE,{"disambiguationData":[TD([makeQuery(id+"F1.opExtrude","SWEPT_FACE",FACE,{"disambiguationData":[OSD([subQ6])]})])],"derivedFrom":makeQuery(id+"F1.opExtrude","CAP_FACE",FACE,{"disambiguationData":[OSD([subQ6,subQ8,subQ9,subQ7,subQ4,subQ3,subQ2,subQ1,subQ0,subQ5,subQ10,subQ11])],"isStart":true})});}
            var sketch = newSketch(context, id + "F16", { "sketchPlane" : qUnion([Q0])});
            skCircle(sketch, "E79.0", {"center": v(60, 67.5) * mm, "radius": 4 * mm});
            skLineSegment(sketch, "E79.1", {"start": v(80, -80) * mm, "end": v(80, 80) * mm});
            skArc(sketch, "E79.2", {"start": v(80, 80) * mm, "mid": v(77.07, 87.07) * mm, "end": v(70, 90) * mm});
            skLineSegment(sketch, "E79.3", {"start": v(-70, 90) * mm, "end": v(70, 90) * mm});
            skCircle(sketch, "E79.4", {"center": v(60, -67.5) * mm, "radius": 4 * mm});
            skArc(sketch, "E79.5", {"start": v(70, -90) * mm, "mid": v(77.07, -87.07) * mm, "end": v(80, -80) * mm});
            skLineSegment(sketch, "E79.6", {"start": v(60, 40.3) * mm, "end": v(60, -40.3) * mm});
            skLineSegment(sketch, "E79.7", {"start": v(-70, -90) * mm, "end": v(70, -90) * mm});
            skArc(sketch, "E79.8", {"start": v(-56.15, -48.18) * mm, "mid": v(0, -67.5) * mm, "end": v(56.15, -48.18) * mm});
            skArc(sketch, "E79.9", {"start": v(56.15, -48.18) * mm, "mid": v(58.99, -44.68) * mm, "end": v(60, -40.3) * mm});
            skCircle(sketch, "E79.10", {"center": v(-60, -67.5) * mm, "radius": 4 * mm});
            skArc(sketch, "E79.11", {"start": v(-80, -80) * mm, "mid": v(-77.07, -87.07) * mm, "end": v(-70, -90) * mm});
            skArc(sketch, "E79.12", {"start": v(-60, -40.3) * mm, "mid": v(-58.99, -44.68) * mm, "end": v(-56.15, -48.18) * mm});
            skLineSegment(sketch, "E79.13", {"start": v(-60, 40.3) * mm, "end": v(-60, -40.3) * mm});
            skLineSegment(sketch, "E79.14", {"start": v(-80, -80) * mm, "end": v(-80, 80) * mm});
            skArc(sketch, "E79.15", {"start": v(-70, 90) * mm, "mid": v(-77.07, 87.07) * mm, "end": v(-80, 80) * mm});
            skArc(sketch, "E79.16", {"start": v(-56.15, 48.18) * mm, "mid": v(-58.99, 44.68) * mm, "end": v(-60, 40.3) * mm});
            skArc(sketch, "E79.17", {"start": v(56.15, 48.18) * mm, "mid": v(0, 67.5) * mm, "end": v(-56.15, 48.18) * mm});
            skCircle(sketch, "E79.18", {"center": v(-60, 67.5) * mm, "radius": 4 * mm});
            skArc(sketch, "E79.19", {"start": v(60, 40.3) * mm, "mid": v(58.99, 44.68) * mm, "end": v(56.15, 48.18) * mm});
            skLineSegment(sketch, "E80", {"start": v(-33, 90) * mm, "end": v(-15, 108) * mm});
            skLineSegment(sketch, "E81", {"start": v(-15, 108) * mm, "end": v(-15, 120) * mm});
            skLineSegment(sketch, "E82", {"start": v(33, 90) * mm, "end": v(15, 108) * mm});
            skLineSegment(sketch, "E83", {"start": v(15, 108) * mm, "end": v(15, 120) * mm});
            skLineSegment(sketch, "E84", {"start": v(0, 90) * mm, "end": v(0, 120) * mm, "construction": true});
            skCircle(sketch, "E85", {"center": v(0, 120) * mm, "radius": 6 * mm});
            skArc(sketch, "E86", {"start": v(15, 120) * mm, "mid": v(0, 135) * mm, "end": v(-15, 120) * mm});
            skLineSegment(sketch, "E87", {"start": v(-80, 0) * mm, "end": v(80, 0) * mm, "construction": true});
            skArc(sketch, "E88.MirrorCS", {"start": v(-15, 120) * mm, "mid": v(0, 135) * mm, "end": v(15, 120) * mm});
            skLineSegment(sketch, "E89.MirrorCS", {"start": v(80, 0) * mm, "end": v(-80, 0) * mm, "construction": true});
            skLineSegment(sketch, "E90.MirrorCS", {"start": v(70, 90) * mm, "end": v(-70, 90) * mm});
            skCircle(sketch, "E91.MirrorC", {"center": v(0, -120) * mm, "radius": 6 * mm});
            skArc(sketch, "E92.MirrorCS", {"start": v(15, -120) * mm, "mid": v(0, -135) * mm, "end": v(-15, -120) * mm});
            skLineSegment(sketch, "E93.MirrorCS", {"start": v(15, -108) * mm, "end": v(15, -120) * mm});
            skLineSegment(sketch, "E94.MirrorCS", {"start": v(33, -90) * mm, "end": v(15, -108) * mm});
            skLineSegment(sketch, "E95.MirrorCS", {"start": v(-15, -108) * mm, "end": v(-15, -120) * mm});
            skLineSegment(sketch, "E96.MirrorCS", {"start": v(-33, -90) * mm, "end": v(-15, -108) * mm});
            skLineSegment(sketch, "E97.MirrorCS", {"start": v(0, -90) * mm, "end": v(0, -120) * mm, "construction": true});
            skSolve(sketch);
        }
        {
            var Q0;
            Q0 = qSketchRegion(id + "F16", true);
            var Q1;
            Q1=makeQuery(id+"F2.opExtrude","CAP_FACE",FACE,{"disambiguationData":[OSD([sQuery(id+"F0.wireOp",EDGE,"E12"),sQuery(id+"F0.wireOp",EDGE,"E13"),sQuery(id+"F0.wireOp",EDGE,"E14"),sQuery(id+"F0.wireOp",EDGE,"E15"),sQuery(id+"F0.wireOp",EDGE,"E17.filletArc"),sQuery(id+"F0.wireOp",EDGE,"E18.filletArc"),sQuery(id+"F0.wireOp",EDGE,"E19.filletArc"),sQuery(id+"F0.wireOp",EDGE,"E20.filletArc"),sQuery(id+"F0.wireOp",EDGE,"E25.0"),sQuery(id+"F0.wireOp",EDGE,"E25.1"),sQuery(id+"F0.wireOp",EDGE,"E25.2"),sQuery(id+"F0.wireOp",EDGE,"E25.3"),sQuery(id+"F0.wireOp",EDGE,"E25.4"),sQuery(id+"F0.wireOp",EDGE,"E25.5"),sQuery(id+"F0.wireOp",EDGE,"E25.6"),sQuery(id+"F0.wireOp",EDGE,"E25.7")])],"isStart":false});
            extrude(context, id + "F17", {"entities" : qUnion([Q0]), "endBound" : BoundingType.UP_TO_SURFACE, "depth" : 25 * mm, "endBoundEntityFace" : qUnion([Q1]), "offsetDistance" : 25 * mm});
        }
    });
